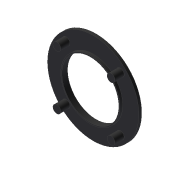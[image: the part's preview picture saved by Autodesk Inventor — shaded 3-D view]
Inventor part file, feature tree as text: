
AUTODESK INVENTOR PART (.ipt)
format: ipt  version: 2017 (Build 210142000, 142)  size: 112,128 bytes
history: native  units: mm
features: extrude x4, sketch x4, pattern_circular x1, projected_geometry x1
ambient origin geometry x8: Origin, YZ Plane, XZ Plane, XY Plane, X Axis, Y Axis, Z Axis, Center Point
bodies: Solid1 (feature_tree)
feature tree (10):
  extrude  "Extrusion1"  Depth=2.0mm TaperAngle=0.0deg
  extrude  "Extrusion2"  Depth=40.0mm
  extrude  "Extrusion3"  Depth=2.0mm TaperAngle=0.0deg
  extrude  "Extrusion4"  Depth=6.5mm
  pattern_circular  "Circular Pattern1"  [2 undecoded]
  sketch  "Sketch1"  dims[d0=64.0mm d1=2.0mm d2=0.0mm]
  sketch  "Sketch2"  dims[d3=41.5mm d4=40.0mm]
  sketch  "Sketch3"  dims[d5=2.0mm d6=0.0mm d7=2.0mm d8=0.0mm]
  projected_geometry  "Projected Loop1"
  sketch  "Sketch4"  dims[d9=5.5mm d10=19.0mm d11=19.0mm d12=6.5mm d13=0.0mm d14=40.0mm d15=360.0deg]
note: 2 required parameter values undecoded (feature->parameter linkage not recoverable at this tier; creation-order binding heuristic only, values carry confidence <= 0.55)
